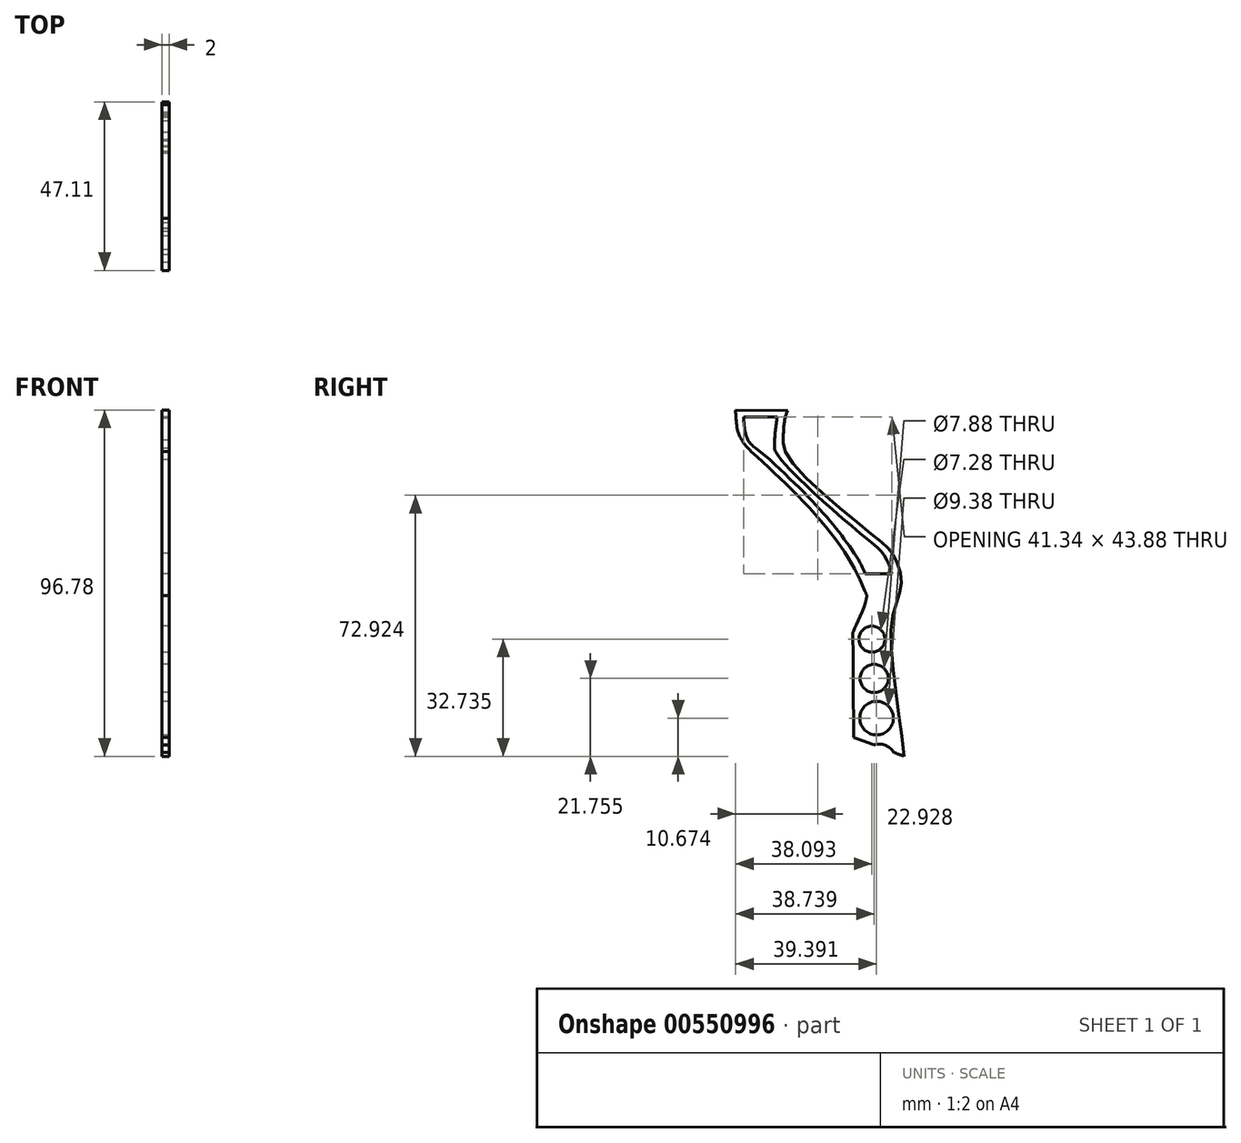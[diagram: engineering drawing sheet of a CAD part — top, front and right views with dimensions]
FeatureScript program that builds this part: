
annotation { "Feature Type Name" : "Feature", "Feature Type Description" : "" }
export const myFeature = defineFeature(function(context is Context, id is Id, definition is map)
    precondition{}
    {
        {
            var Q0;
            Q0=qCreatedBy(makeId("Right.planeOp"),FACE);
            var sketch = newSketch(context, id + "F0", { "sketchPlane" : qUnion([Q0])});
            skPoint(sketch, "E0", {"position": v(-128.73, 82.44) * mm});
            skPoint(sketch, "E1", {"position": v(28.72, 75.42) * mm});
            skPoint(sketch, "E2", {"position": v(18.39, 63.44) * mm});
            skPoint(sketch, "E3", {"position": v(75.42, 17.15) * mm});
            skPoint(sketch, "E4", {"position": v(75.42, -22.94) * mm});
            skPoint(sketch, "E5", {"position": v(94.43, -31.2) * mm});
            skPoint(sketch, "E6", {"position": v(94.43, -51.86) * mm});
            skLineSegment(sketch, "E7", {"start": v(27.45, 73.94) * mm, "end": v(18.39, 63.44) * mm});
            skPoint(sketch, "E8", {"position": v(24.38, 70.39) * mm});
            skFitSpline(sketch, "E9", {"points": [v(-128.73, 82.44) * mm, v(-12.68, 78.46) * mm, v(28.72, 75.42) * mm], "startDerivative": vector(208.84, -5.82) * mm, "endDerivative": vector(96.65, -8.45) * mm});
            skFitSpline(sketch, "E10", {"points": [v(75.42, -22.94) * mm, v(91.68, -29) * mm, v(94.43, -31.2) * mm, v(94.43, -51.86) * mm], "startDerivative": vector(49.63, -18.32) * mm, "endDerivative": vector(-4.17, -61.24) * mm});
            skLineSegment(sketch, "E11", {"start": v(75.42, 9.61) * mm, "end": v(75.42, -21.54) * mm});
            skFitSpline(sketch, "E12", {"points": [v(10.43, 76.95) * mm, v(10.68, 70.48) * mm, v(18.39, 63.44) * mm, v(41.4, 37.3) * mm, v(52.46, 20.6) * mm, v(75.42, 17.15) * mm], "startDerivative": vector(-6.66, -55.67) * mm, "endDerivative": vector(115.26, 0.34) * mm});
            skFitSpline(sketch, "E13", {"points": [v(18.39, 63.44) * mm, v(39.53, 35.88) * mm, v(52.46, 20.6) * mm], "startDerivative": vector(39.23, -52.2) * mm, "endDerivative": vector(28.4, -32.57) * mm});
            skFitSpline(sketch, "E14", {"points": [v(39.53, 35.88) * mm, v(48.66, 24.39) * mm], "startDerivative": vector(9.14, -11.49) * mm, "endDerivative": vector(9.14, -11.49) * mm});
            skFitSpline(sketch, "E15", {"points": [v(70.05, 24.75) * mm, v(74.2, 17.67) * mm, v(75.42, 9.61) * mm], "startDerivative": vector(9.75, -13.63) * mm, "endDerivative": vector(1, -16.65) * mm});
            skArc(sketch, "E16.filletArc", {"start": v(75.42, -21.54) * mm, "mid": v(75.78, -22.69) * mm, "end": v(76.73, -23.42) * mm});
            skFitSpline(sketch, "E17", {"points": [v(23.56, 69.43) * mm, v(49.14, 48.39) * mm, v(70.05, 24.75) * mm], "startDerivative": vector(52.63, -39.98) * mm, "endDerivative": vector(40.3, -49.4) * mm});
            skArc(sketch, "E18.filletArc", {"start": v(27.45, 73.94) * mm, "mid": v(27.62, 74.97) * mm, "end": v(26.78, 75.59) * mm});
            skFitSpline(sketch, "E19", {"points": [v(75.42, 5.47) * mm, v(58.4, 5.26) * mm, v(51.58, 2.37) * mm, v(47.65, -9) * mm, v(46.82, -13.13) * mm, v(48.27, -15.2) * mm, v(75.42, -16.44) * mm], "startDerivative": vector(-87.15, 1.4) * mm, "endDerivative": vector(130.13, 2.89) * mm});
            skFitSpline(sketch, "E20", {"points": [v(62.73, 5.5) * mm, v(54.68, 2.16) * mm, v(47.65, -9) * mm], "startDerivative": vector(-19.14, -4.54) * mm, "endDerivative": vector(-11.3, -23.76) * mm});
            skLineSegment(sketch, "E21.top", {"start": v(34.13, 60.9) * mm, "end": v(34.63, 60.9) * mm});
            skPoint(sketch, "E22.visualSharp", {"position": v(67.13, 84.49) * mm});
            skArc(sketch, "E22.filletArc", {"start": v(67.13, 82.49) * mm, "mid": v(66.54, 83.9) * mm, "end": v(65.13, 84.49) * mm});
            skPoint(sketch, "E23.visualSharp", {"position": v(32.13, 60.9) * mm});
            skArc(sketch, "E23.filletArc", {"start": v(32.13, 62.9) * mm, "mid": v(32.71, 61.48) * mm, "end": v(34.13, 60.9) * mm});
            skPoint(sketch, "E21.bottom.start.orphan", {"position": v(32.13, 84.49) * mm});
            skFitSpline(sketch, "E24", {"points": [v(42.9, 60.96) * mm, v(58.87, 46.48) * mm, v(74.35, 28.3) * mm, v(80.5, 16.26) * mm], "startDerivative": vector(44.88, -38.7) * mm, "endDerivative": vector(17.7, -41.42) * mm});
            skFitSpline(sketch, "E25", {"points": [v(78.85, 20.1) * mm, v(80.5, 16.26) * mm, v(76.85, 6.48) * mm, v(76.59, 4.13) * mm, v(76.73, -48.95) * mm], "startDerivative": vector(18.22, -20.9) * mm, "endDerivative": vector(-0.26, -138.73) * mm});
            skFitSpline(sketch, "E26", {"points": [v(57.54, 61.14) * mm, v(58.13, 55.57) * mm, v(82.24, 33.07) * mm, v(87.93, 27.37) * mm, v(90.13, 19.77) * mm, v(87.5, 8.82) * mm, v(90.7, -26.54) * mm, v(91.68, -49.77) * mm], "startDerivative": vector(-14.65, -54.98) * mm, "endDerivative": vector(-0.75, -120.7) * mm});
            skLineSegment(sketch, "E27.bottom", {"start": v(76.73, -48.95) * mm, "end": v(91.64, -48.95) * mm});
            skLineSegment(sketch, "E27.top", {"start": v(76.73, -40.28) * mm, "end": v(76.74, -40.28) * mm});
            skLineSegment(sketch, "E27.left", {"start": v(76.73, -48.95) * mm, "end": v(76.73, -40.28) * mm});
            skLineSegment(sketch, "E27.right", {"start": v(91.64, -48.95) * mm, "end": v(91.64, -40.28) * mm});
            skArc(sketch, "E28.filletArc", {"start": v(80.1, 14.27) * mm, "mid": v(80.3, 15.98) * mm, "end": v(79.9, 17.66) * mm});
            skFitSpline(sketch, "E29", {"points": [v(54.78, 59.15) * mm, v(54.78, 56.87) * mm, v(57.57, 53.05) * mm, v(63.98, 46.54) * mm, v(80.72, 31.87) * mm, v(83.4, 29.7) * mm, v(86.2, 26.08) * mm, v(87.43, 22.26) * mm], "startDerivative": vector(-4.6, -25.33) * mm, "endDerivative": vector(7.32, -33.09) * mm});
            skLineSegment(sketch, "E30", {"start": v(87.43, 22.26) * mm, "end": v(80.82, 22.26) * mm});
            skPoint(sketch, "E31.1.internal.orphan", {"position": v(79.58, 24.75) * mm});
            skFitSpline(sketch, "E32", {"points": [v(77, 28.05) * mm, v(78.54, 25.54) * mm, v(79.76, 22.98) * mm, v(79.96, 22.26) * mm], "startDerivative": vector(3.84, -5.9) * mm, "endDerivative": vector(0.63, -3) * mm});
            skLineSegment(sketch, "E33", {"start": v(80.82, 22.26) * mm, "end": v(79.96, 22.26) * mm});
            skCircle(sketch, "E34", {"center": v(81.92, 4.01) * mm, "radius": 3.64 * mm});
            skCircle(sketch, "E35", {"center": v(82.57, -6.97) * mm, "radius": 3.94 * mm});
            skCircle(sketch, "E36", {"center": v(83.22, -18.05) * mm, "radius": 4.69 * mm});
            skFitSpline(sketch, "E37", {"points": [v(48.16, 56.42) * mm, v(44.87, 60.96) * mm, v(43.83, 68.06) * mm], "startDerivative": vector(-8.2, 8.8) * mm, "endDerivative": vector(-0.61, 14.37) * mm});
            skFitSpline(sketch, "E38", {"points": [v(57.13, 59.58) * mm, v(57.54, 65.2) * mm, v(58.38, 67.93) * mm], "startDerivative": vector(0.33, 10.52) * mm, "endDerivative": vector(2.28, 5.92) * mm});
            skLineSegment(sketch, "E39", {"start": v(58.38, 67.93) * mm, "end": v(43.83, 68.06) * mm});
            skLineSegment(sketch, "E40", {"start": v(57.13, 59.58) * mm, "end": v(57.15, 58.74) * mm});
            skLineSegment(sketch, "E41", {"start": v(49.84, 54.91) * mm, "end": v(48.16, 56.42) * mm});
            skFitSpline(sketch, "E42", {"points": [v(51.09, 56.34) * mm, v(47.4, 59.5) * mm, v(46.15, 64.5) * mm, v(46.09, 66.15) * mm], "startDerivative": vector(-11.08, 6.69) * mm, "endDerivative": vector(-0.06, 6.14) * mm});
            skFitSpline(sketch, "E43", {"points": [v(54.78, 56.87) * mm, v(54.78, 60.3) * mm, v(55.42, 65.73) * mm], "startDerivative": vector(-0.25, 7.33) * mm, "endDerivative": vector(1.46, 10.28) * mm});
            skLineSegment(sketch, "E44", {"start": v(46.09, 66.15) * mm, "end": v(55.53, 66.06) * mm});
            skLineSegment(sketch, "E45", {"start": v(55.53, 66.06) * mm, "end": v(55.42, 65.73) * mm});
            skLineSegment(sketch, "E46", {"start": v(49.57, 57.3) * mm, "end": v(53.47, 54.1) * mm});
            skFitSpline(sketch, "E47.trimOffspring", {"points": [v(48.07, 59.15) * mm, v(68.21, 39.41) * mm, v(77, 28.05) * mm], "startDerivative": vector(38.44, -35.72) * mm, "endDerivative": vector(18.29, -25.93) * mm});
            skArc(sketch, "E48.filletArc", {"start": v(54.77, 57.22) * mm, "mid": v(54.83, 56.81) * mm, "end": v(54.97, 56.42) * mm});
            skCircle(sketch, "E49", {"center": v(83.92, -29.97) * mm, "radius": 4.69 * mm});
            skCircle(sketch, "E50", {"center": v(84.61, -41.68) * mm, "radius": 4.69 * mm});
            skSolve(sketch);
        }
        {
            var Q0;
            Q0=makeQuery(id+"F0.imprint","IMPRINT",FACE,{"disambiguationData":[TD([[makeQuery(id+"F0.imprint","IMPRINT",EDGE,{"derivedFrom":sQuery(id+"F0.wireOp",EDGE,"E24")}),1.0]])]});
            extrude(context, id + "F1", {"entities" : qUnion([Q0]), "depth" : 2 * mm, "offsetDistance" : 25 * mm});
        }
    });
